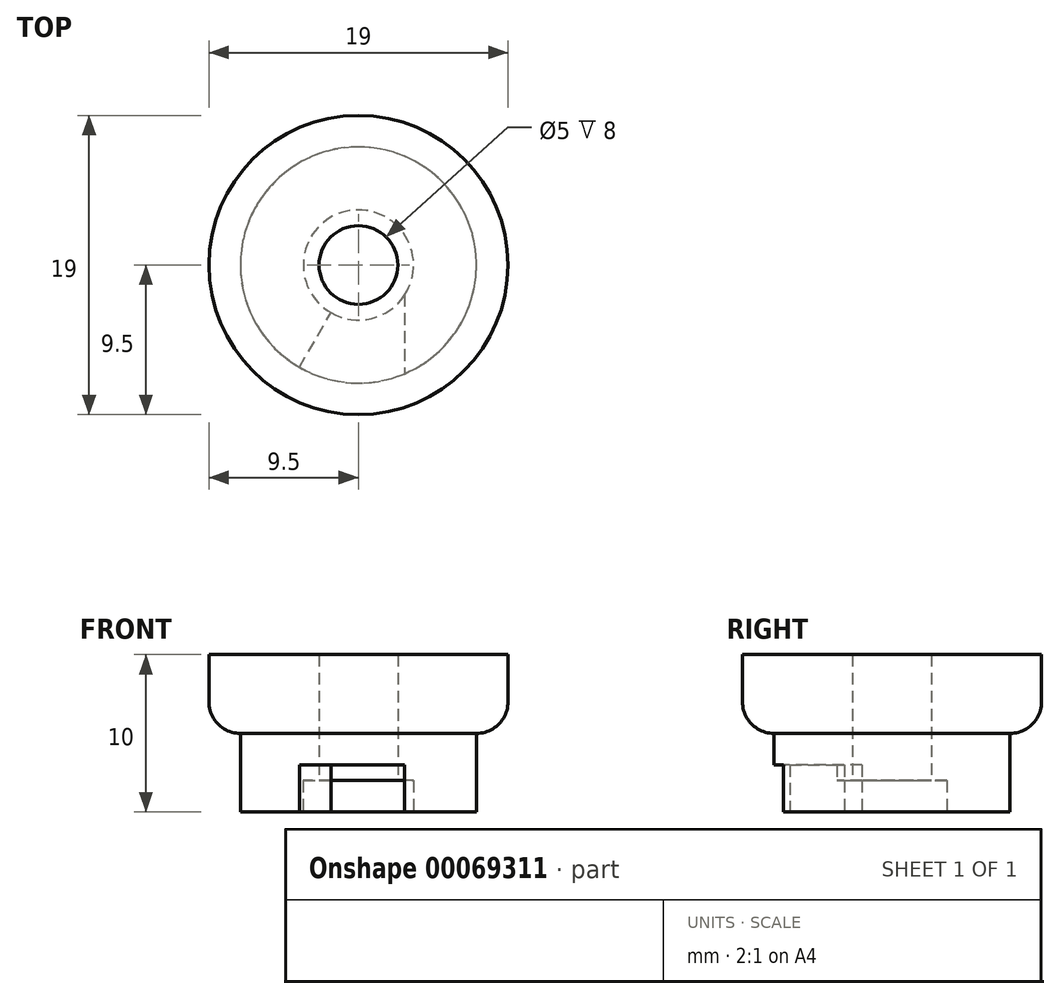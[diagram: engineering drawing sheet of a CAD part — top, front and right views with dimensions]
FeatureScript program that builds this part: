
annotation { "Feature Type Name" : "Feature", "Feature Type Description" : "" }
export const myFeature = defineFeature(function(context is Context, id is Id, definition is map)
    precondition{}
    {
        {
            var Q0;
            Q0=qCreatedBy(makeId("Front.planeOp"),FACE);
            var sketch = newSketch(context, id + "F0", { "sketchPlane" : qUnion([Q0])});
            skLineSegment(sketch, "E0", {"start": v(3.5, 2) * mm, "end": v(3.5, 0) * mm});
            skLineSegment(sketch, "E1", {"start": v(3.5, 0) * mm, "end": v(7.5, 0) * mm});
            skLineSegment(sketch, "E2", {"start": v(7.5, 0) * mm, "end": v(7.5, 5) * mm});
            skLineSegment(sketch, "E3", {"start": v(7.5, 5) * mm, "end": v(9.5, 5) * mm});
            skLineSegment(sketch, "E4", {"start": v(9.5, 5) * mm, "end": v(9.5, 10) * mm});
            skLineSegment(sketch, "E5", {"start": v(3.5, 2) * mm, "end": v(2.5, 2) * mm});
            skLineSegment(sketch, "E6", {"start": v(2.5, 2) * mm, "end": v(2.5, 10) * mm});
            skLineSegment(sketch, "E7", {"start": v(2.5, 10) * mm, "end": v(9.5, 10) * mm});
            skLineSegment(sketch, "E8", {"start": v(0, 0) * mm, "end": v(0, 17.61) * mm, "construction": true});
            skSolve(sketch);
        }
        {
            var Q0;
            Q0 = qSketchRegion(id + "FMapNWMc4amiS7J_0", true);
            var Q1;
            Q1=makeQuery(id+"F0.imprint","IMPRINT",FACE,{"disambiguationData":[TD([[makeQuery(id+"F0.imprint","IMPRINT",EDGE,{"derivedFrom":sQuery(id+"F0.wireOp",EDGE,"E0")}),1.0]])]});
            var Q2;
            Q2=sQuery(id+"F0.wireOp",EDGE,"E8");
            revolve(context, id + "F1", {"entities" : qUnion([Q0, Q1]), "axis" : qUnion([Q2]), "revolveType" : RevolveType.FULL});
        }
        {
            var Q0;
            Q0=makeQuery(id+"F1.opRevolve","SWEPT_EDGE",EDGE,{"disambiguationData":[OSD([sQuery(id+"F0.wireOp",EDGE,"E3"),sQuery(id+"F0.wireOp",EDGE,"E4")])]});
            fillet(context, id + "F2", {"entities" : qUnion([Q0]), "radius" : 2 * mm, "tangentPropagation" : true, "allowEdgeOverflow" : false});
        }
        {
            var Q0;
            Q0=makeQuery(id+"F1.opRevolve","SWEPT_FACE",FACE,{"disambiguationData":[OSD([sQuery(id+"F0.wireOp",EDGE,"E1")])]});
            var sketch = newSketch(context, id + "F3", { "sketchPlane" : qUnion([Q0])});
            skLineSegment(sketch, "E9", {"start": v(2.94, 1.9) * mm, "end": v(2.94, 6.9) * mm});
            skArc(sketch, "E10", {"start": v(2.94, 1.9) * mm, "mid": v(0.82, 3.4) * mm, "end": v(-1.75, 3.03) * mm});
            skArc(sketch, "E11", {"start": v(2.94, 6.9) * mm, "mid": v(-0.45, 7.49) * mm, "end": v(-3.75, 6.5) * mm});
            skLineSegment(sketch, "E12", {"start": v(0, 0) * mm, "end": v(-3.75, 6.5) * mm, "construction": true});
            skLineSegment(sketch, "E13", {"start": v(-3.75, 6.5) * mm, "end": v(-1.75, 3.03) * mm});
            skSolve(sketch);
        }
        {
            var Q0;
            Q0=makeQuery(id+"F3.imprint","IMPRINT",FACE,{"disambiguationData":[TD([[makeQuery(id+"F3.imprint","IMPRINT",EDGE,{"derivedFrom":sQuery(id+"F3.wireOp",EDGE,"E9")}),1.0]])]});
            extrude(context, id + "F4", {"entities" : qUnion([Q0]), "operationType" : NewBodyOperationType.REMOVE, "oppositeDirection" : true, "depth" : 3 * mm});
        }
    });
